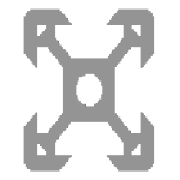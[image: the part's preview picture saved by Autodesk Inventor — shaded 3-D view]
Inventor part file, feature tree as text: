
AUTODESK INVENTOR PART (.ipt)
format: ipt  version: 2017.3 (Build 213256000, 256)  size: 195,584 bytes
history: native  units: mm
features: other x3, sketch x3, plane x1
ambient origin geometry x8: Origin, YZ Plane, XZ Plane, XY Plane, X Axis, Y Axis, Z Axis, Center Point
bodies: Solid1 (feature_tree), Body (feature_tree)
feature tree (7):
  other  "Driven Length"
  other  "Start Plane"
  other  "End Plane"
  sketch  "Sketch1"  dims[d2=4.2mm]
  sketch  "Sketch4"  dims[d3=1.5mm]
  plane  "Work Plane4"
  sketch  "Sketch5"  dims[d4=1.64mm d5=1.8mm d6=5.68mm d7=1.8mm d9=1.5mm d12=-0.0mm d13=400.0mm d14=0.13mm d15=0.0mm d18=90.0deg d17=400.0mm]
